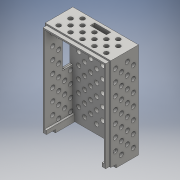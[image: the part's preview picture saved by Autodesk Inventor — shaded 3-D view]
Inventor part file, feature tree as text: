
AUTODESK INVENTOR PART (.ipt)
format: ipt  version: 2016 (Build 200138000, 138)  size: 637,440 bytes
history: native  units: mm
features: sketch x19, extrude x13, hole x3
ambient origin geometry x8: Origin, YZ Plane, XZ Plane, XY Plane, X Axis, Y Axis, Z Axis, Center Point
bodies: Solid1 (feature_tree)
feature tree (35):
  extrude  "Extrusion1"  Depth=60.0mm
  extrude  "Extrusion3"  Depth=6.0mm
  extrude  "Extrusion5"  Depth=90.0mm
  extrude  "Extrusion7"  Depth=27.0mm
  sketch  "Sketch9"  dims[d13=4.3mm d17=15.0mm]
  sketch  "Sketch10"  dims[d18=27.0mm d19=45.0mm]
  extrude  "Extrusion8"  Depth=15.0mm
  extrude  "Extrusion9"  Depth=45.0mm
  extrude  "Extrusion10"  Depth=90.0mm
  sketch  "Sketch14"  dims[d33=1.5mm d34=0.0mm d40=63.0mm]
  sketch  "Sketch16"  dims[d41=1.5mm d42=30.0mm d43=0.0mm]
  hole  "Hole3"  [1 undecoded]
  hole  "Hole4"  [1 undecoded]
  extrude  "Extrusion12"  Depth=63.0mm
  extrude  "Extrusion13"  Depth=1.5mm TaperAngle=0.0deg
  sketch  "Sketch19"  dims[d50=3.0mm d51=3.0mm]
  extrude  "Extrusion14"  Depth=4.3mm
  sketch  "Sketch21"  dims[d62=3.8mm d63=7.5mm]
  extrude  "Extrusion16"  Depth=3.0mm
  extrude  "Extrusion17"  Depth=3.0mm
  extrude  "Extrusion18"  Depth=3.0mm
  hole  "Hole5"  [1 undecoded]
  sketch  "Sketch1"  dims[d0=60.0mm d1=4.3mm]
  sketch  "Sketch3"  dims[d2=6.0mm d3=6.0mm]
  sketch  "Sketch5"  dims[d6=90.0mm d7=4.3mm]
  sketch  "Sketch8"  dims[d10=15.0mm d12=27.0mm]
  sketch  "Sketch11"  dims[d20=1.5mm d21=0.0mm d25=90.0mm]
  sketch  "Sketch12"  dims[d26=30.0mm d27=1.5mm d28=0.0mm]
  sketch  "Sketch13"  dims[d31=90.0mm d32=30.0mm]
  sketch  "Sketch17"  dims[d46=7.5mm d47=4.3mm]
  sketch  "Sketch18"  dims[d48=6.0mm d49=3.0mm]
  sketch  "Sketch20"  dims[d52=3.0mm d53=3.0mm]
  sketch  "Sketch22"  dims[d64=4.3mm]
  sketch  "Sketch23"  dims[d65=6.0mm]
  sketch  "Sketch24"  dims[d66=4.3mm d67=6.0mm d69=3.0mm d70=3.0mm d71=3.0mm d72=3.0mm d80=30.0mm d81=0.0mm d82=3.7mm d83=2.0mm d84=0.0mm d85=3.7mm d86=2.0mm d87=0.0mm d99=4.35mm d100=6.0mm d101=4.0mm d102=2.0mm d103=90.0deg d104=8.0mm d105=20.594885mm d106=4.35mm d107=6.0mm d108=4.0mm d109=2.0mm d110=90.0deg d111=8.0mm d112=20.594885mm d114=10.0mm d115=0.0mm d116=3.65mm d117=4.35mm d118=4.35mm d119=4.35mm d120=4.35mm d121=4.35mm d122=4.35mm d123=4.35mm d124=4.35mm d125=4.35mm d126=4.35mm d127=1.5mm d128=0.0mm d129=4.35mm d130=4.35mm d131=1.5mm d132=0.0mm d135=1.5mm d136=0.0mm d137=9.0mm d138=3.0mm d139=0.0mm d140=1.5mm d141=0.0mm d142=4.35mm d143=6.0mm d144=4.0mm d145=2.0mm d146=90.0deg d147=8.0mm d148=20.594885mm]
note: 3 required parameter values undecoded (feature->parameter linkage not recoverable at this tier; creation-order binding heuristic only, values carry confidence <= 0.55)
